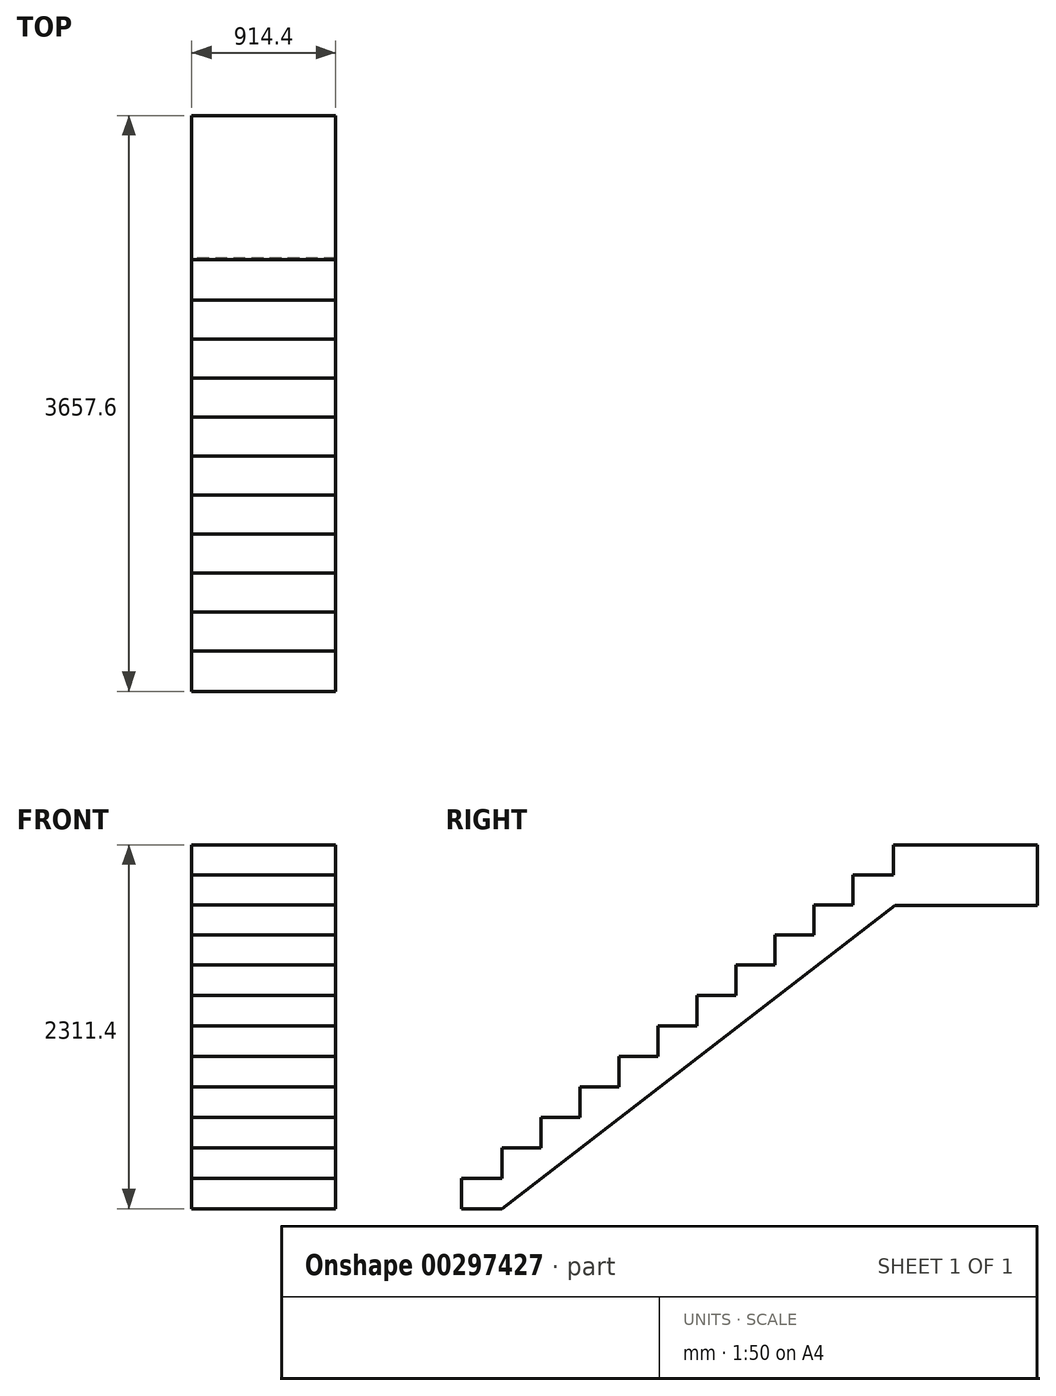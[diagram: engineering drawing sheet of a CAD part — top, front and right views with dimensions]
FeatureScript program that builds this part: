
annotation { "Feature Type Name" : "Feature", "Feature Type Description" : "" }
export const myFeature = defineFeature(function(context is Context, id is Id, definition is map)
    precondition{}
    {
        {
            var Q0;
            Q0=qCreatedBy(makeId("Right.planeOp"),FACE);
            var sketch = newSketch(context, id + "F0", { "sketchPlane" : qUnion([Q0])});
            skLineSegment(sketch, "E0", {"start": v(-363.72, 347.57) * mm, "end": v(-363.72, 541.25) * mm});
            skLineSegment(sketch, "E1", {"start": v(-363.72, 541.25) * mm, "end": v(-116.07, 541.25) * mm});
            skLineSegment(sketch, "E2", {"start": v(-116.07, 541.25) * mm, "end": v(-116.07, 734.92) * mm});
            skLineSegment(sketch, "E3", {"start": v(-116.07, 734.92) * mm, "end": v(131.58, 734.92) * mm});
            skLineSegment(sketch, "E4", {"start": v(131.58, 734.92) * mm, "end": v(131.58, 928.6) * mm});
            skLineSegment(sketch, "E5", {"start": v(131.58, 928.6) * mm, "end": v(379.23, 928.6) * mm});
            skLineSegment(sketch, "E6", {"start": v(379.23, 928.6) * mm, "end": v(379.23, 1122.27) * mm});
            skLineSegment(sketch, "E7", {"start": v(379.23, 1122.27) * mm, "end": v(626.88, 1122.27) * mm});
            skLineSegment(sketch, "E8", {"start": v(626.88, 1122.27) * mm, "end": v(626.88, 1315.95) * mm});
            skLineSegment(sketch, "E9", {"start": v(626.88, 1315.95) * mm, "end": v(874.53, 1315.95) * mm});
            skLineSegment(sketch, "E10", {"start": v(874.53, 1315.95) * mm, "end": v(874.53, 1509.62) * mm});
            skLineSegment(sketch, "E11", {"start": v(874.53, 1509.62) * mm, "end": v(1122.18, 1509.62) * mm});
            skLineSegment(sketch, "E12", {"start": v(1122.18, 1509.62) * mm, "end": v(1122.18, 1703.3) * mm});
            skLineSegment(sketch, "E13", {"start": v(1122.18, 1703.3) * mm, "end": v(1369.83, 1703.3) * mm});
            skLineSegment(sketch, "E14", {"start": v(1369.83, 1703.3) * mm, "end": v(1369.83, 1893.8) * mm});
            skLineSegment(sketch, "E15", {"start": v(1369.83, 1893.8) * mm, "end": v(1617.48, 1893.8) * mm});
            skLineSegment(sketch, "E16", {"start": v(1617.48, 1893.8) * mm, "end": v(1617.48, 2084.3) * mm});
            skLineSegment(sketch, "E17", {"start": v(1617.48, 2084.3) * mm, "end": v(1865.13, 2084.3) * mm});
            skLineSegment(sketch, "E18", {"start": v(1865.13, 2084.3) * mm, "end": v(1865.13, 2274.8) * mm});
            skLineSegment(sketch, "E19", {"start": v(1865.13, 2274.8) * mm, "end": v(2122.3, 2274.8) * mm});
            skLineSegment(sketch, "E20", {"start": v(2122.3, 2274.8) * mm, "end": v(2122.3, 2465.3) * mm});
            skLineSegment(sketch, "E21", {"start": v(2122.3, 2465.3) * mm, "end": v(3036.7, 2465.3) * mm});
            skLineSegment(sketch, "E22", {"start": v(3036.7, 2081.12) * mm, "end": v(3036.7, 2465.3) * mm});
            skLineSegment(sketch, "E23", {"start": v(-363.72, 347.57) * mm, "end": v(-620.9, 347.57) * mm});
            skLineSegment(sketch, "E24", {"start": v(-620.9, 347.57) * mm, "end": v(-620.9, 153.9) * mm});
            skLineSegment(sketch, "E25", {"start": v(-620.9, 153.9) * mm, "end": v(-363.72, 153.9) * mm});
            skLineSegment(sketch, "E26", {"start": v(-363.72, 153.9) * mm, "end": v(2131.83, 2081.12) * mm});
            skLineSegment(sketch, "E27", {"start": v(2131.83, 2081.12) * mm, "end": v(3036.7, 2081.12) * mm});
            skSolve(sketch);
        }
        {
            var Q0;
            Q0 = qSketchRegion(id + "F0", true);
            extrude(context, id + "F1", {"entities" : qUnion([Q0]), "depth" : 914.4 * mm, "offsetDistance" : 25.4 * mm});
        }
    });
